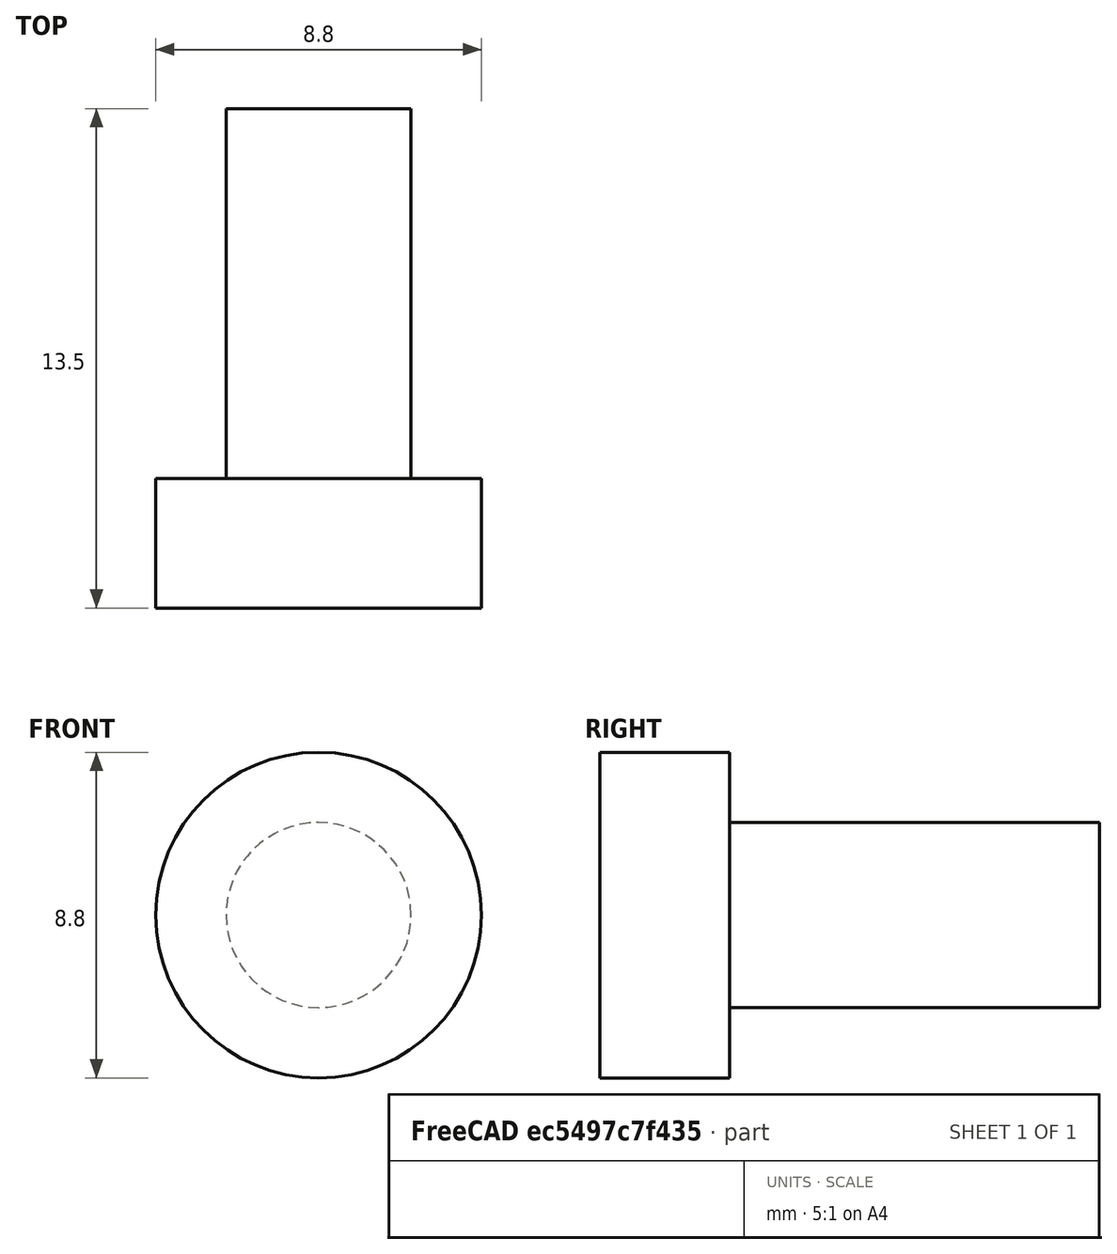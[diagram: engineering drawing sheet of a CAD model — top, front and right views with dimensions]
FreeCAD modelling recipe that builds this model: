
FCSTD DOCUMENT  (FreeCAD 1.0R39319 (Git))
Label: visM5L10
License: All rights reserved
LicenseURL: https://en.wikipedia.org/wiki/All_rights_reserved
objects: Sketcher::SketchObject×1, PartDesign::Revolution×1, PartDesign::Body×1
note: 6 computed .brp shape members not serialized (recipe doc carries the construction recipe); baked Part::Feature solids carry a one-line shape summary decoded from their .brp

FEATURE [Sketcher::SketchObject] Sketch
  ArcFitTolerance = 1e-06
  AttachmentSupport = -> [YZ_Plane]
  FullyConstrained = true
  MakeInternals = false
  MapMode = 5
  Placement = pos=(0,0,0) rot=(0.57735,0.57735,0.57735;2.0944rad)
  sketch-geometry (6):
    g0: LineSegment StartX=-3.5 StartY=0 StartZ=0 EndX=-3.5 EndY=4.4 EndZ=0
    g1: LineSegment StartX=-3.5 StartY=4.4 StartZ=0 EndX=0 EndY=4.4 EndZ=0
    g2: LineSegment StartX=0 StartY=4.4 StartZ=0 EndX=0 EndY=2.5 EndZ=0
    g3: LineSegment StartX=0 StartY=2.5 StartZ=0 EndX=10 EndY=2.5 EndZ=0
    g4: LineSegment StartX=10 StartY=0 StartZ=0 EndX=10 EndY=2.5 EndZ=0
    g5: LineSegment StartX=-3.5 StartY=0 StartZ=0 EndX=10 EndY=0 EndZ=0
  constraints (18):
    c: PointOnObject(g0,g-1)
    c: Vertical(g0)
    c: Coincident(g1,g0)
    c: PointOnObject(g1,g-2)
    c: Horizontal(g1)
    c: Coincident(g2,g1)
    c: PointOnObject(g2,g-2)
    c: Coincident(g3,g2)
    c: Horizontal(g3)
    c: PointOnObject(g4,g-1)
    c: Coincident(g5,g0)
    c: Coincident(g5,g4)
    c: Coincident(g4,g3)
    c: Perpendicular(g-1,g4)
    c: DistanceY(g0,g0) = 4.4
    c: DistanceX(g1,g1) = 3.5
    c: DistanceX(g3,g3) = 10
    c: DistanceY(g4,g4) = 2.5
FEATURE [PartDesign::Revolution] Revolution
  Angle = 360
  Angle2 = 60
  Axis = (1e-16,1,-1e-16)
  Base = (0,0,0)
  Placement = pos=(0,0,0) rot=(1,1,1;2.0944rad)
  Profile = -> Sketch
  ReferenceAxis = -> Y_Axis
  Refine = true
  Suppressed = false
  Type = 0
FEATURE [PartDesign::Body] Body  label="Corps"
  AllowCompound = false
  Group = -> [Sketch,Revolution]
  Origin = -> Origin
  Tip = -> Revolution
